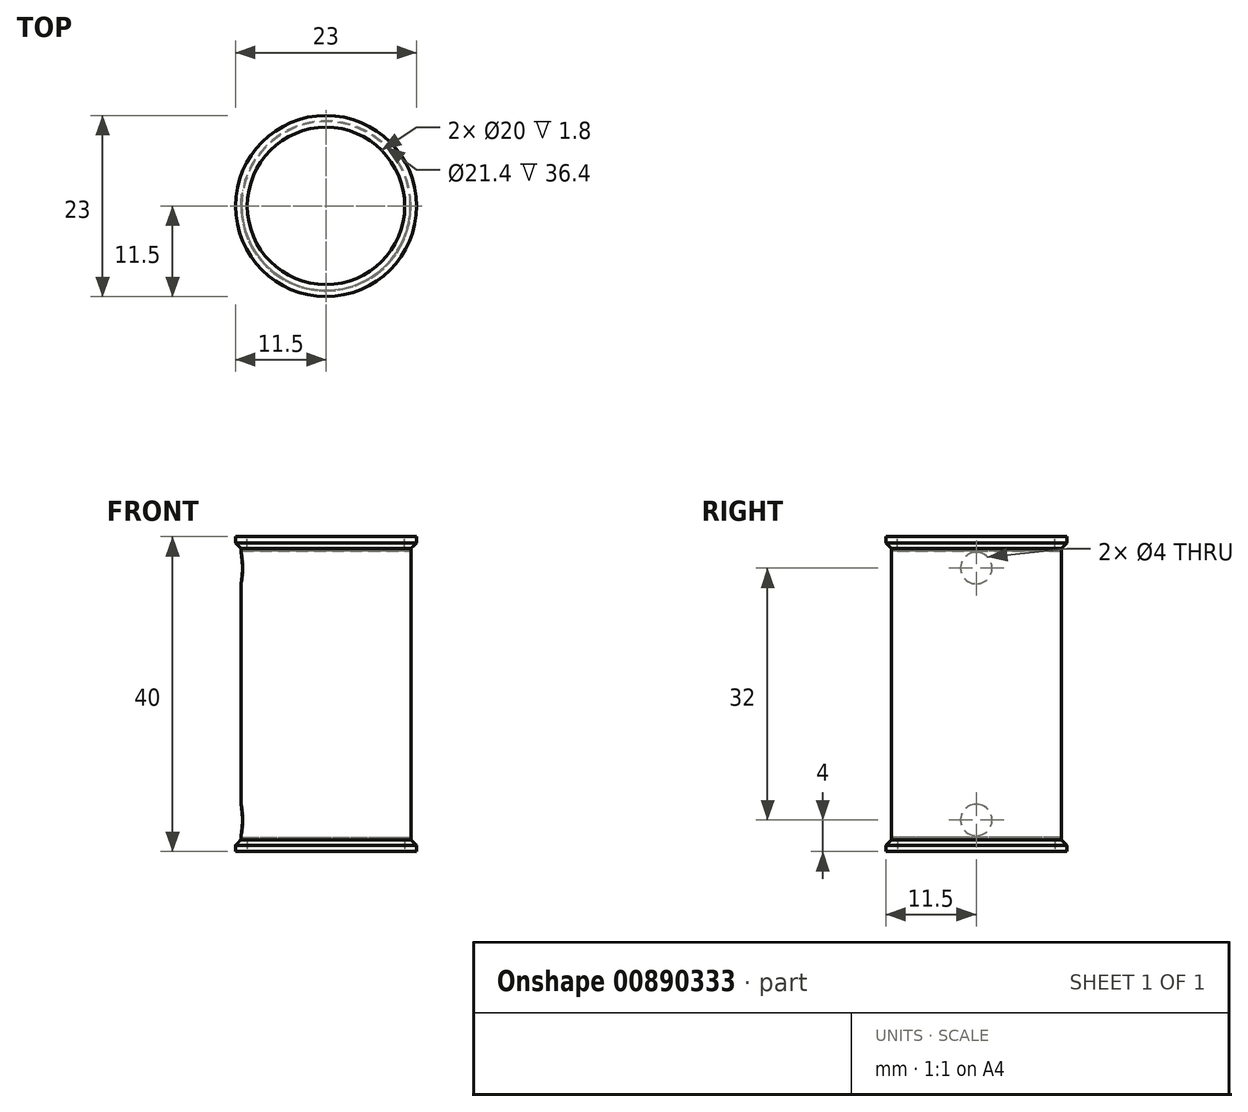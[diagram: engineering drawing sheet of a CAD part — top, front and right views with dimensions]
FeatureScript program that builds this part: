
annotation { "Feature Type Name" : "Feature", "Feature Type Description" : "" }
export const myFeature = defineFeature(function(context is Context, id is Id, definition is map)
    precondition{}
    {
        {
            var Q0;
            Q0=qCreatedBy(makeId("Top.planeOp"),FACE);
            var sketch = newSketch(context, id + "F0", { "sketchPlane" : qUnion([Q0])});
            skCircle(sketch, "E0", {"center": v(0, 0) * mm, "radius": 10.7 * mm});
            skCircle(sketch, "E1", {"center": v(0, 0) * mm, "radius": 10.8 * mm});
            skSolve(sketch);
        }
        {
            var Q0;
            Q0 = qSketchRegion(id + "F0", true);
            extrude(context, id + "F1", {"entities" : qUnion([Q0]), "depth" : 20 * mm, "offsetDistance" : 25 * mm, "hasSecondDirection" : true, "secondDirectionOppositeDirection" : true, "secondDirectionDepth" : 20 * mm});
        }
        {
            var Q0;
            Q0=qCreatedBy(makeId("Right.planeOp"),FACE);
            var sketch = newSketch(context, id + "F2", { "sketchPlane" : qUnion([Q0])});
            skLineSegment(sketch, "E2", {"start": v(0, 0) * mm, "end": v(0, 16) * mm, "construction": true});
            skCircle(sketch, "E3", {"center": v(0, 16) * mm, "radius": 2 * mm});
            skLineSegment(sketch, "E4", {"start": v(0, 0) * mm, "end": v(-3.17, 0) * mm, "construction": true});
            skCircle(sketch, "E5.MirrorC", {"center": v(0, -16) * mm, "radius": 2 * mm});
            skSolve(sketch);
        }
        {
            var Q0;
            Q0 = qSketchRegion(id + "F2", true);
            extrude(context, id + "F3", {"entities" : qUnion([Q0]), "operationType" : NewBodyOperationType.REMOVE, "oppositeDirection" : true, "depth" : 25 * mm, "offsetDistance" : 25 * mm});
        }
        {
            var Q0;
            Q0=makeQuery(id+"F1.opExtrude","CAP_FACE",FACE,{"disambiguationData":[OSD([sQuery(id+"F0.wireOp",EDGE,"E0"),sQuery(id+"F0.wireOp",EDGE,"E1")])],"isStart":false});
            var sketch = newSketch(context, id + "F4", { "sketchPlane" : qUnion([Q0])});
            skCircle(sketch, "E6", {"center": v(0, 0) * mm, "radius": 10 * mm});
            skCircle(sketch, "E7", {"center": v(0, 0) * mm, "radius": 11.5 * mm});
            skSolve(sketch);
        }
        {
            var Q0;
            Q0 = qSketchRegion(id + "F4", true);
            extrude(context, id + "F5", {"entities" : qUnion([Q0]), "operationType" : NewBodyOperationType.ADD, "oppositeDirection" : true, "depth" : 1.8 * mm, "offsetDistance" : 25 * mm});
        }
        {
            var Q0;
            Q0=makeQuery(id+"F1.opExtrude","CAP_FACE",FACE,{"disambiguationData":[OSD([sQuery(id+"F0.wireOp",EDGE,"E0"),sQuery(id+"F0.wireOp",EDGE,"E1")])],"isStart":true});
            var sketch = newSketch(context, id + "F6", { "sketchPlane" : qUnion([Q0])});
            skCircle(sketch, "E8", {"center": v(0, 0) * mm, "radius": 10 * mm});
            skCircle(sketch, "E9", {"center": v(0, 0) * mm, "radius": 11.5 * mm});
            skSolve(sketch);
        }
        {
            var Q0;
            Q0 = qSketchRegion(id + "F6", true);
            extrude(context, id + "F7", {"entities" : qUnion([Q0]), "operationType" : NewBodyOperationType.ADD, "oppositeDirection" : true, "depth" : 1.8 * mm, "offsetDistance" : 25 * mm});
        }
        {
            var Q0;
            Q0=makeQuery(id+"F7.opExtrude","CAP_EDGE",EDGE,{"disambiguationData":[OSD([sQuery(id+"F6.wireOp",EDGE,"E9")])],"isStart":false});
            var Q1;
            Q1=makeQuery(id+"F5.opExtrude","CAP_EDGE",EDGE,{"disambiguationData":[OSD([sQuery(id+"F4.wireOp",EDGE,"E7")])],"isStart":false});
            chamfer(context, id + "F8", {"entities" : qUnion([Q0, Q1]), "width" : 1 * mm, "tangentPropagation" : true});
        }
    });
